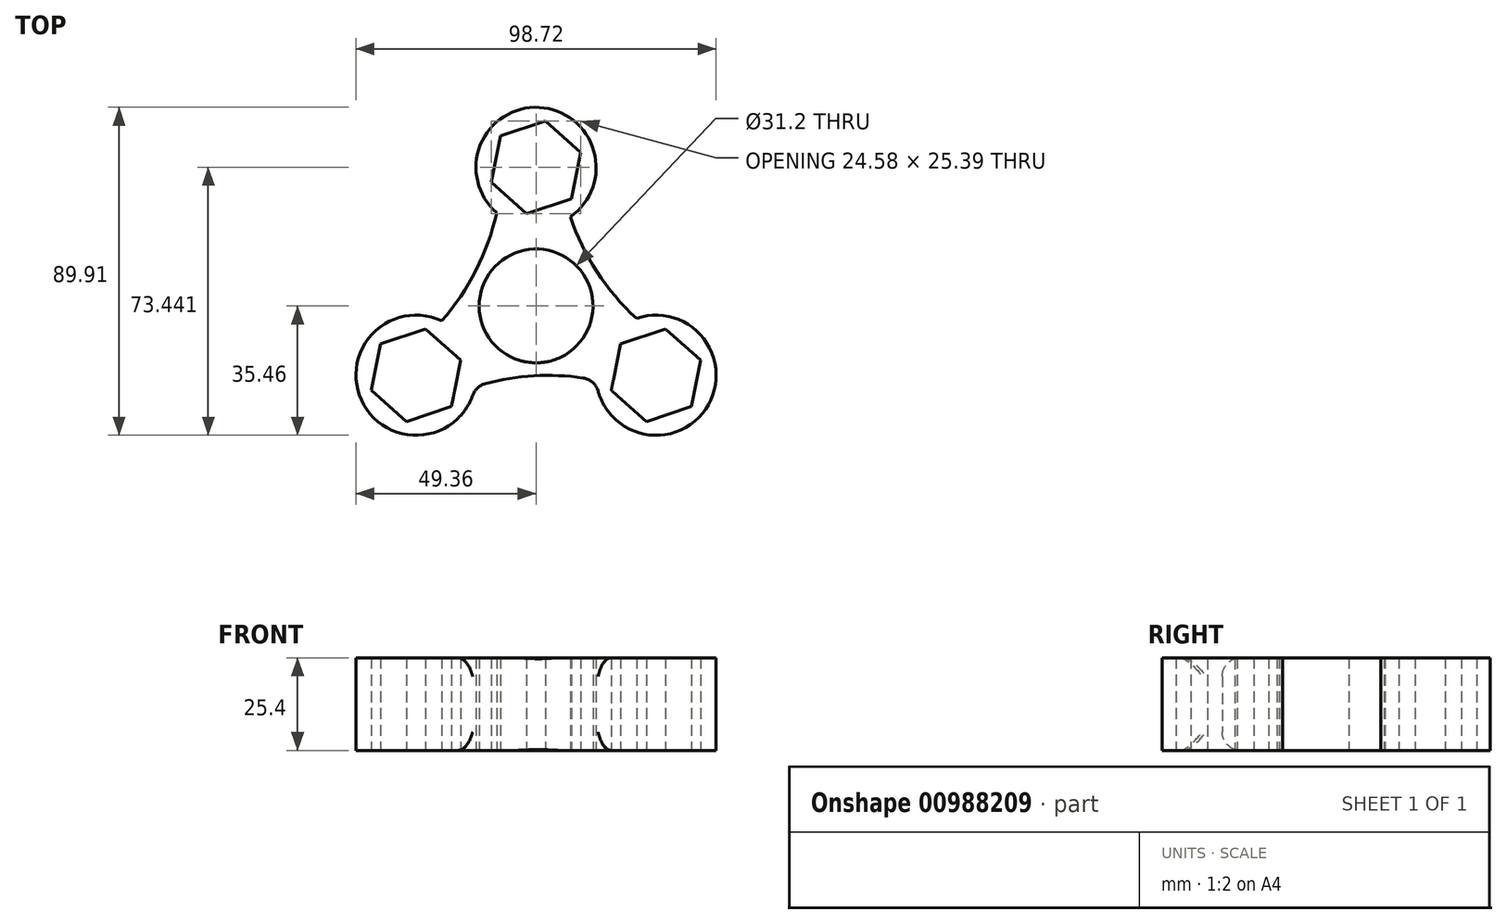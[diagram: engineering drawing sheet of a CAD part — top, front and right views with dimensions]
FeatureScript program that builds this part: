
annotation { "Feature Type Name" : "Feature", "Feature Type Description" : "" }
export const myFeature = defineFeature(function(context is Context, id is Id, definition is map)
    precondition{}
    {
        {
            var Q0;
            Q0=qCreatedBy(makeId("Top.planeOp"),FACE);
            var sketch = newSketch(context, id + "F0", { "sketchPlane" : qUnion([Q0])});
            skCircle(sketch, "E0", {"center": v(0, 0) * mm, "radius": 15.6 * mm});
            skCircle(sketch, "E1.cCircle", {"center": v(0, 37.98) * mm, "radius": 11.22 * mm, "construction": true});
            skLineSegment(sketch, "E1.0", {"start": v(-12.3, 33.88) * mm, "end": v(-9.7, 46.57) * mm});
            skLineSegment(sketch, "E1.1", {"start": v(-9.7, 46.57) * mm, "end": v(2.6, 50.68) * mm});
            skLineSegment(sketch, "E1.2", {"start": v(2.6, 50.68) * mm, "end": v(12.3, 42.08) * mm});
            skLineSegment(sketch, "E1.3", {"start": v(12.3, 42.08) * mm, "end": v(9.7, 29.39) * mm});
            skLineSegment(sketch, "E1.4", {"start": v(9.7, 29.39) * mm, "end": v(-2.6, 25.29) * mm});
            skLineSegment(sketch, "E1.5", {"start": v(-2.6, 25.29) * mm, "end": v(-12.3, 33.88) * mm});
            skPoint(sketch, "E1.0.midPoint", {"position": v(-11, 40.23) * mm});
            skPoint(sketch, "E2.1.0", {"position": v(-29.34, -29.63) * mm});
            skLineSegment(sketch, "E2.1.1", {"start": v(-45.18, -23.1) * mm, "end": v(-42.6, -10.4) * mm});
            skLineSegment(sketch, "E2.1.2", {"start": v(-20.6, -14.89) * mm, "end": v(-23.2, -27.58) * mm});
            skLineSegment(sketch, "E2.1.3", {"start": v(-42.6, -10.4) * mm, "end": v(-30.3, -6.3) * mm});
            skLineSegment(sketch, "E2.1.4", {"start": v(-30.3, -6.3) * mm, "end": v(-20.6, -14.89) * mm});
            skCircle(sketch, "E2.1.5", {"center": v(-32.9, -19) * mm, "radius": 11.22 * mm, "construction": true});
            skLineSegment(sketch, "E2.1.6", {"start": v(-23.2, -27.58) * mm, "end": v(-35.49, -31.69) * mm});
            skLineSegment(sketch, "E2.1.7", {"start": v(-35.49, -31.69) * mm, "end": v(-45.18, -23.1) * mm});
            skPoint(sketch, "E2.2.0", {"position": v(40.33, -10.6) * mm});
            skLineSegment(sketch, "E2.2.1", {"start": v(42.6, -27.58) * mm, "end": v(30.3, -31.69) * mm});
            skLineSegment(sketch, "E2.2.2", {"start": v(23.2, -10.4) * mm, "end": v(35.49, -6.3) * mm});
            skLineSegment(sketch, "E2.2.3", {"start": v(30.3, -31.69) * mm, "end": v(20.6, -23.1) * mm});
            skLineSegment(sketch, "E2.2.4", {"start": v(20.6, -23.1) * mm, "end": v(23.2, -10.4) * mm});
            skCircle(sketch, "E2.2.5", {"center": v(32.9, -19) * mm, "radius": 11.22 * mm, "construction": true});
            skLineSegment(sketch, "E2.2.6", {"start": v(35.49, -6.3) * mm, "end": v(45.18, -14.89) * mm});
            skLineSegment(sketch, "E2.2.7", {"start": v(45.18, -14.89) * mm, "end": v(42.6, -27.58) * mm});
            skArc(sketch, "E3", {"start": v(-29.04, -7.4) * mm, "mid": v(-16.1, 10.48) * mm, "end": v(-9.77, 31.64) * mm});
            skArc(sketch, "E4.1.0", {"start": v(20.94, -21.45) * mm, "mid": v(-1.03, -19.18) * mm, "end": v(-22.52, -24.28) * mm});
            skArc(sketch, "E4.2.0", {"start": v(8.1, 28.86) * mm, "mid": v(17.13, 8.7) * mm, "end": v(32.29, -7.36) * mm});
            skCircle(sketch, "E5", {"center": v(0, 37.98) * mm, "radius": 16.47 * mm});
            skArc(sketch, "E6.1.0", {"start": v(-25.88, -4.08) * mm, "mid": v(-47.58, -26.44) * mm, "end": v(-16.72, -22.14) * mm});
            skCircle(sketch, "E6.2.0", {"center": v(32.9, -19) * mm, "radius": 16.47 * mm});
            skSolve(sketch);
        }
        {
            var Q0;
            Q0 = qSketchRegion(id + "F0", true);
            extrude(context, id + "F1", {"entities" : qUnion([Q0]), "depth" : 25.4 * mm, "offsetDistance" : 25.4 * mm});
        }
        {
            var Q0;
            Q0=makeQuery(id+"F1.opExtrude","SWEPT_FACE",FACE,{"disambiguationData":[OSD([sQuery(id+"F0.wireOp",EDGE,"E4.1.0")])]});
            fillet(context, id + "F2", {"entities" : qUnion([Q0]), "radius" : 5.08 * mm, "tangentPropagation" : true, "allowEdgeOverflow" : false});
        }
    });
